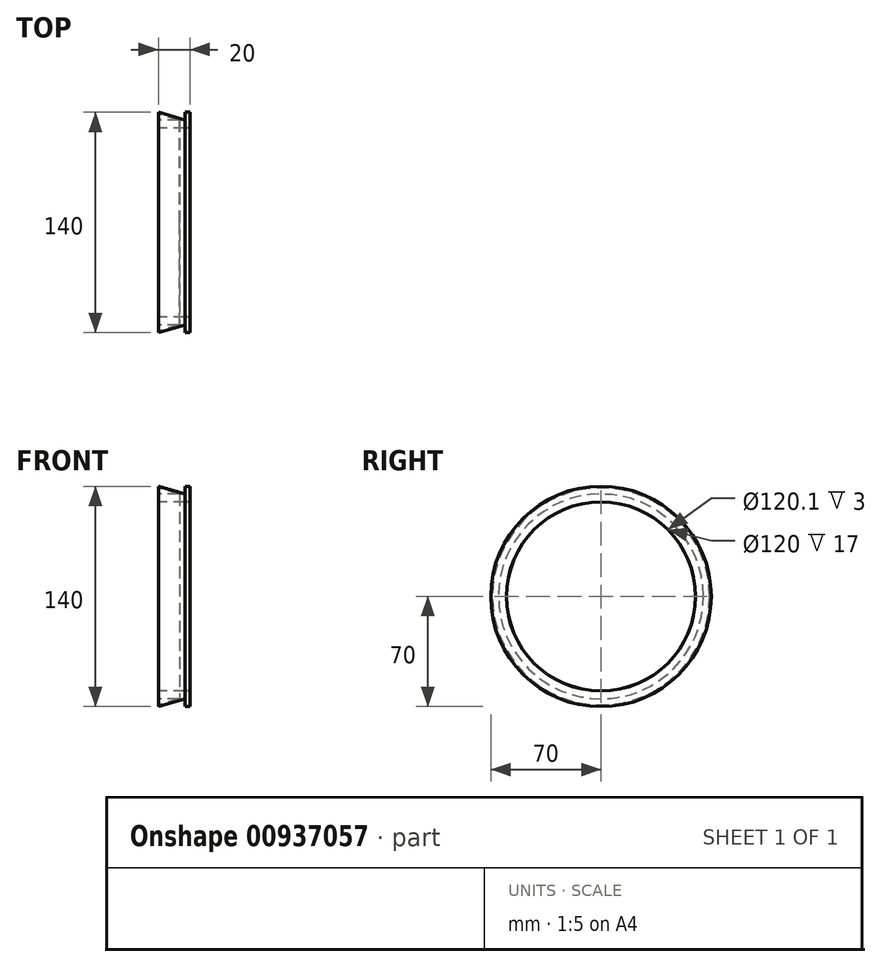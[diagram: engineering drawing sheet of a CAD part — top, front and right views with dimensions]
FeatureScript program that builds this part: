
annotation { "Feature Type Name" : "Feature", "Feature Type Description" : "" }
export const myFeature = defineFeature(function(context is Context, id is Id, definition is map)
    precondition{}
    {
        {
            var Q0;
            Q0=qCreatedBy(makeId("Front.planeOp"),FACE);
            var sketch = newSketch(context, id + "F0", { "sketchPlane" : qUnion([Q0])});
            skLineSegment(sketch, "E0.bottom", {"start": v(-1.5, 70) * mm, "end": v(1.5, 70) * mm});
            skLineSegment(sketch, "E0.top", {"start": v(-1.5, 60.05) * mm, "end": v(1.5, 60.05) * mm});
            skLineSegment(sketch, "E0.left", {"start": v(-1.5, 70) * mm, "end": v(-1.5, 60.05) * mm});
            skLineSegment(sketch, "E0.right", {"start": v(1.5, 70) * mm, "end": v(1.5, 60.05) * mm});
            skLineSegment(sketch, "E1", {"start": v(-46.18, 0) * mm, "end": v(62.63, 0) * mm, "construction": true});
            skSolve(sketch);
        }
        {
            var Q0;
            Q0=makeQuery(id+"F0.imprint","IMPRINT",FACE,{"disambiguationData":[TD([[makeQuery(id+"F0.imprint","IMPRINT",EDGE,{"derivedFrom":sQuery(id+"F0.wireOp",EDGE,"E0.bottom")}),-1.0]])]});
            var Q1;
            Q1=sQuery(id+"F0.wireOp",EDGE,"E1");
            revolve(context, id + "F1", {"surfaceOperationType" : NewSurfaceOperationType.NEW, "entities" : qUnion([Q0]), "axis" : qUnion([Q1]), "revolveType" : RevolveType.FULL});
        }
        {
            var Q0;
            Q0=qCreatedBy(makeId("Front.planeOp"),FACE);
            var sketch = newSketch(context, id + "F2", { "sketchPlane" : qUnion([Q0])});
            skLineSegment(sketch, "E2.bottom", {"start": v(-18.5, 65) * mm, "end": v(-5.04, 65) * mm});
            skLineSegment(sketch, "E2.top", {"start": v(-18.5, 60) * mm, "end": v(-1.5, 60) * mm});
            skLineSegment(sketch, "E2.left", {"start": v(-18.5, 65) * mm, "end": v(-18.5, 60) * mm});
            skLineSegment(sketch, "E2.right", {"start": v(-1.5, 65) * mm, "end": v(-1.5, 60) * mm});
            skLineSegment(sketch, "E3", {"start": v(-1.5, 65) * mm, "end": v(-18.5, 70) * mm});
            skLineSegment(sketch, "E4", {"start": v(-18.5, 68.96) * mm, "end": v(-5.04, 65) * mm});
            skLineSegment(sketch, "E5", {"start": v(-37.45, 0) * mm, "end": v(43.9, 0) * mm, "construction": true});
            skLineSegment(sketch, "E6", {"start": v(-18.5, 70) * mm, "end": v(-18.5, 68.96) * mm});
            skSolve(sketch);
        }
        {
            var Q0;
            Q0=makeQuery(id+"F2.imprint","IMPRINT",FACE,{"disambiguationData":[TD([[makeQuery(id+"F2.imprint","IMPRINT",EDGE,{"derivedFrom":sQuery(id+"F2.wireOp",EDGE,"E2.bottom")}),-1.0]])]});
            var Q1;
            Q1=sQuery(id+"F2.wireOp",EDGE,"E5");
            revolve(context, id + "F3", {"operationType" : NewBodyOperationType.ADD, "surfaceOperationType" : NewSurfaceOperationType.NEW, "entities" : qUnion([Q0]), "axis" : qUnion([Q1]), "revolveType" : RevolveType.FULL});
        }
    });
